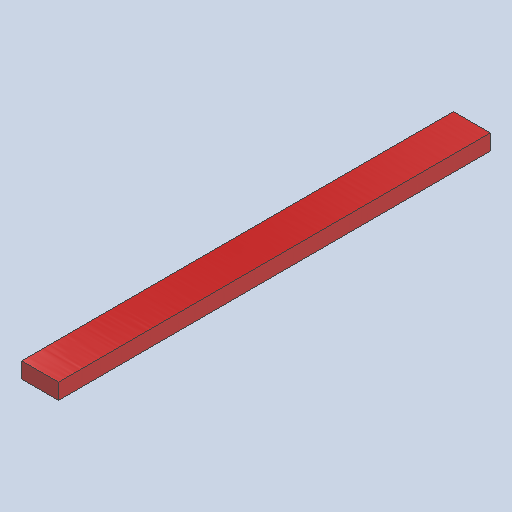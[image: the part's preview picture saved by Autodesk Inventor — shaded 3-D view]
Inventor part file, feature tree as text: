
AUTODESK INVENTOR PART (.ipt)
format: ipt  version: 2025 (Build 290162000, 162)  size: 96,768 bytes
history: native  units: in
note: dims shown in document units (in); Inventor stores cm internally (conversion verified against a paired STEP export)
features: other x3, plane x1, extrude x1, sketch x1
ambient origin geometry x8: Origin, YZ Plane, XZ Plane, XY Plane, X Axis, Y Axis, Z Axis, Center Point
bodies: Solid1 (feature_tree)
feature tree (6):
  plane  "Work Plane1"
  extrude  "Extrusion1"  Depth=3.5in
  sketch  "Sketch1"  dims[d0=1.5in d1=3.5in d2=41.0in d3=0.0in]
  other  "Finish1"
  other  "Assembly2"
  other  "8'x2x4:1"
